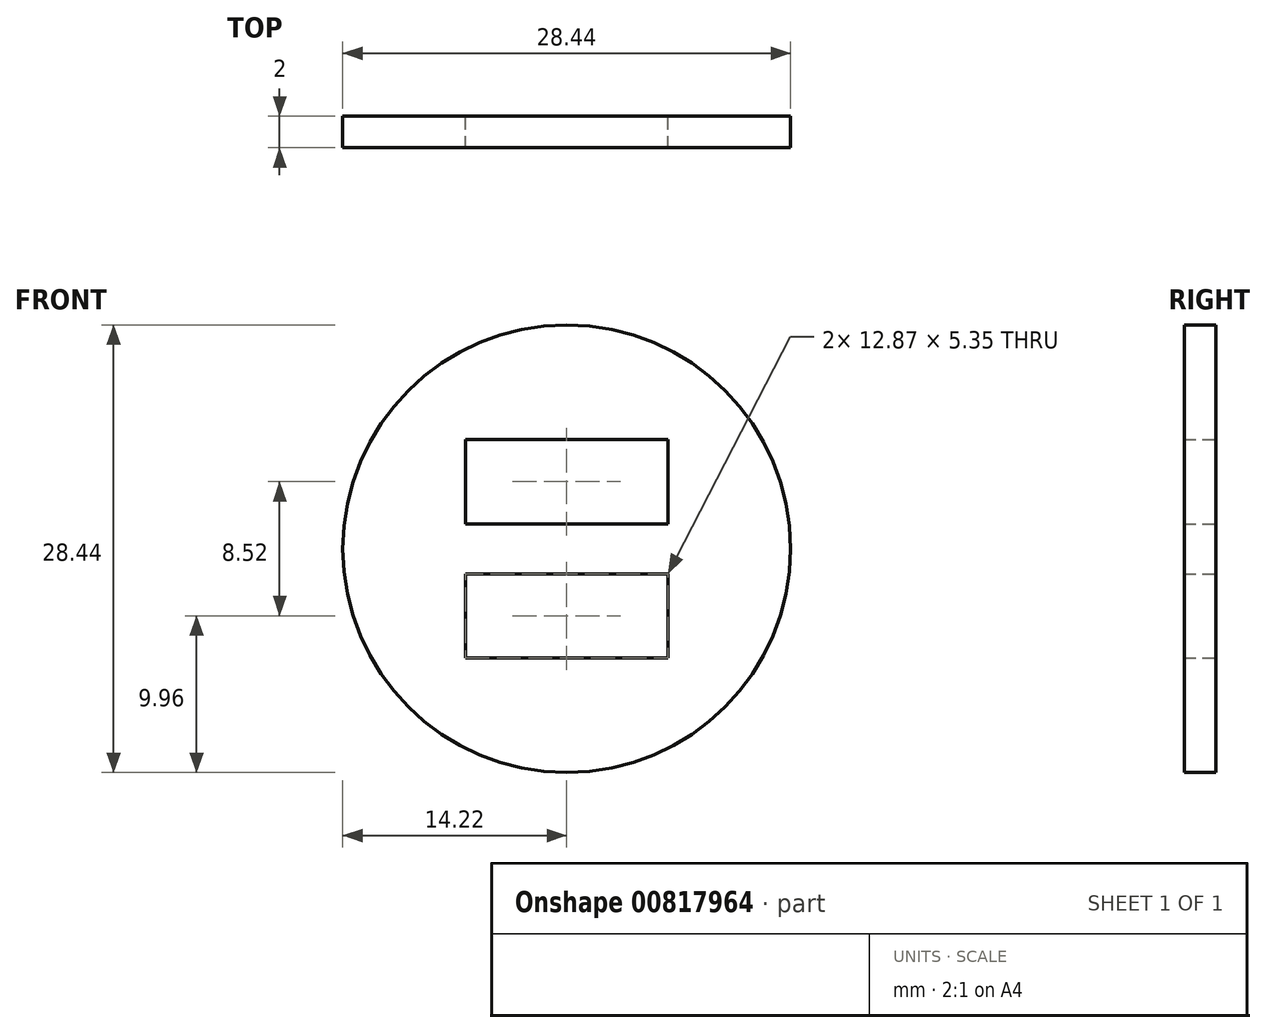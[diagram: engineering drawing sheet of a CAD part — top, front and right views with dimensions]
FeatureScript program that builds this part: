
annotation { "Feature Type Name" : "Feature", "Feature Type Description" : "" }
export const myFeature = defineFeature(function(context is Context, id is Id, definition is map)
    precondition{}
    {
        {
            var Q0;
            Q0=qCreatedBy(makeId("Front.planeOp"),FACE);
            var sketch = newSketch(context, id + "F0", { "sketchPlane" : qUnion([Q0])});
            skCircle(sketch, "E0", {"center": v(0, 0) * mm, "radius": 14.22 * mm});
            skLineSegment(sketch, "E1.bottom", {"start": v(-6.43, 1.58) * mm, "end": v(6.43, 1.58) * mm});
            skLineSegment(sketch, "E1.top", {"start": v(-6.44, 6.93) * mm, "end": v(6.43, 6.93) * mm});
            skLineSegment(sketch, "E1.left", {"start": v(-6.43, 1.58) * mm, "end": v(-6.43, 6.93) * mm});
            skLineSegment(sketch, "E1.right", {"start": v(6.44, 1.58) * mm, "end": v(6.44, 6.93) * mm});
            skPoint(sketch, "E1.middle", {"position": v(0, 4.26) * mm});
            skLineSegment(sketch, "E2.MirrorCS", {"start": v(-6.43, -1.58) * mm, "end": v(6.44, -1.58) * mm});
            skLineSegment(sketch, "E3.MirrorCS", {"start": v(6.44, -1.58) * mm, "end": v(6.43, -6.94) * mm});
            skLineSegment(sketch, "E4.MirrorCS", {"start": v(-6.44, -6.94) * mm, "end": v(6.43, -6.94) * mm});
            skLineSegment(sketch, "E5.MirrorCS", {"start": v(-6.44, -1.58) * mm, "end": v(-6.44, -6.94) * mm});
            skSolve(sketch);
        }
        {
            var Q0;
            Q0=makeQuery(id+"F0.imprint","IMPRINT",FACE,{"disambiguationData":[TD([[makeQuery(id+"F0.imprint","IMPRINT",EDGE,{"derivedFrom":sQuery(id+"F0.wireOp",EDGE,"E0")}),1.0]])]});
            extrude(context, id + "F1", {"entities" : qUnion([Q0]), "depth" : 2 * mm, "offsetDistance" : 25 * mm});
        }
        {
            var Q0;
            Q0=qCreatedBy(makeId("Front.planeOp"),FACE);
            cPlane(context, id + "F2", {"entities" : qUnion([Q0]), "cplaneType" : CPlaneType.OFFSET, "offset" : 3.5 * mm, "oppositeDirection" : true, "width" : 150 * mm, "height" : 150 * mm});
        }
    });
